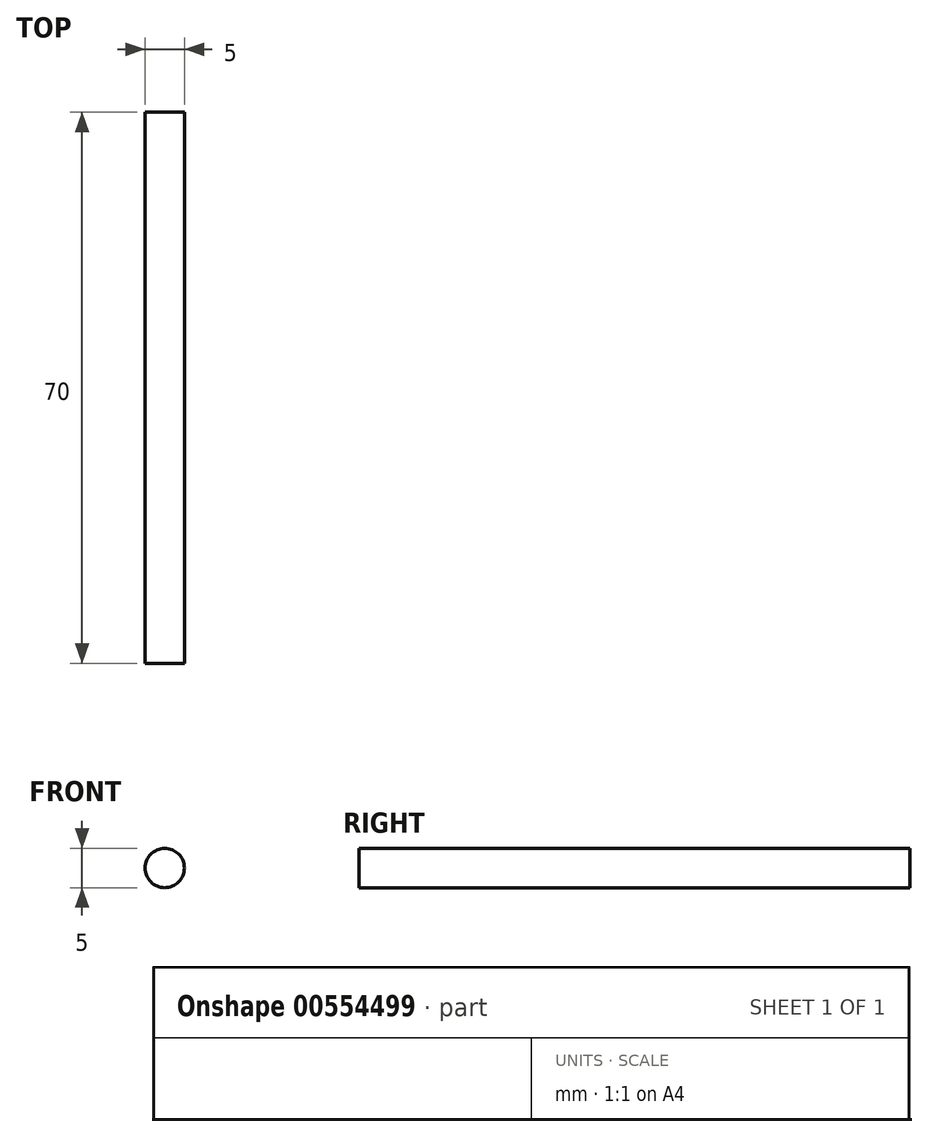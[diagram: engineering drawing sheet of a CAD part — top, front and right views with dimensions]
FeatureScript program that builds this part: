
annotation { "Feature Type Name" : "Feature", "Feature Type Description" : "" }
export const myFeature = defineFeature(function(context is Context, id is Id, definition is map)
    precondition{}
    {
        {
            var Q0;
            Q0=qCreatedBy(makeId("Front.planeOp"),FACE);
            var sketch = newSketch(context, id + "F0", { "sketchPlane" : qUnion([Q0])});
            skCircle(sketch, "E0", {"center": v(0, 0) * mm, "radius": 2.5 * mm});
            skSolve(sketch);
        }
        {
            var Q0;
            Q0 = qSketchRegion(id + "F0", true);
            extrude(context, id + "F1", {"entities" : qUnion([Q0]), "depth" : 70 * mm, "offsetDistance" : 25 * mm});
        }
    });
